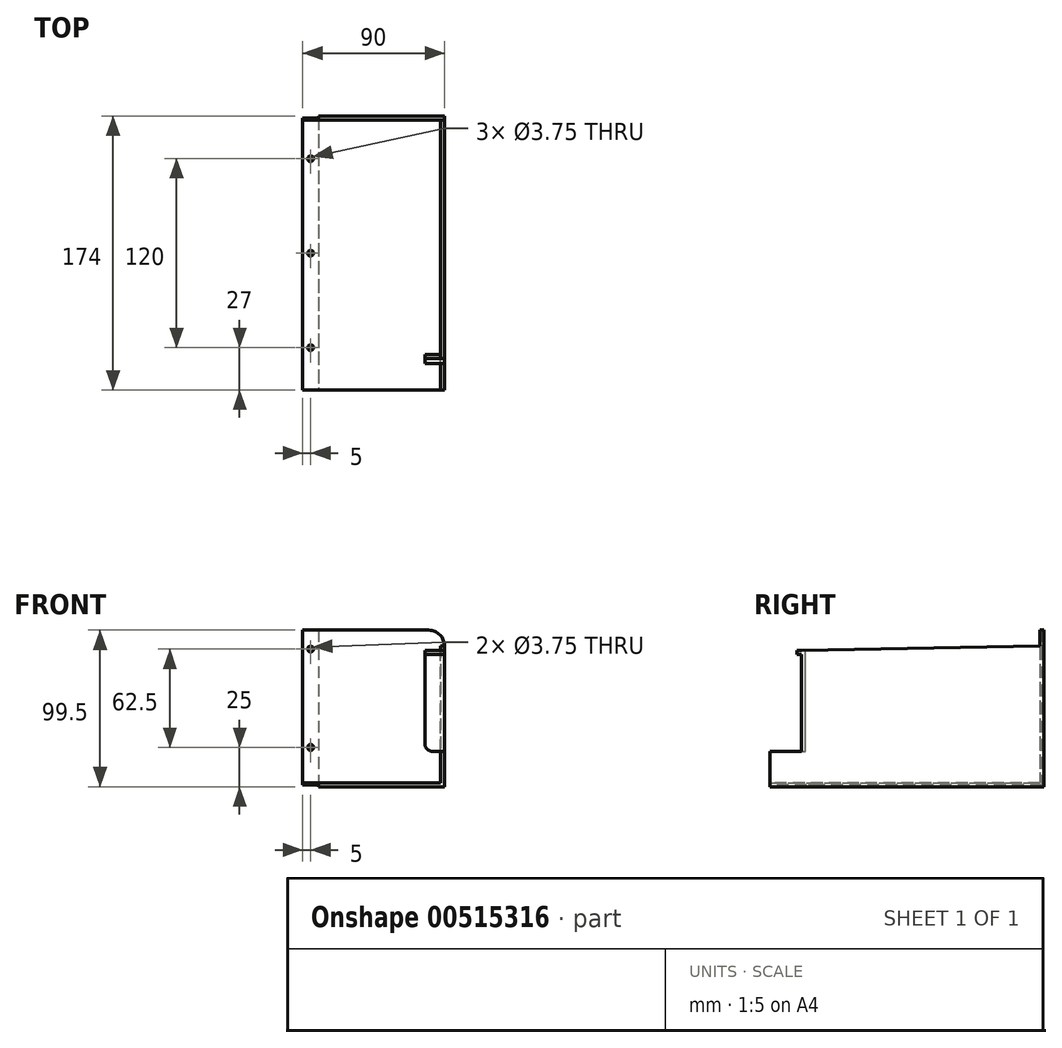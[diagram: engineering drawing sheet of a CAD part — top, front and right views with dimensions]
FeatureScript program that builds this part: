
annotation { "Feature Type Name" : "Feature", "Feature Type Description" : "" }
export const myFeature = defineFeature(function(context is Context, id is Id, definition is map)
    precondition{}
    {
        {
            var Q0;
            Q0=qCreatedBy(makeId("Top.planeOp"),FACE);
            var sketch = newSketch(context, id + "F0", { "sketchPlane" : qUnion([Q0])});
            skLineSegment(sketch, "E0.bottom", {"start": v(0, 87) * mm, "end": v(-80, 87) * mm});
            skLineSegment(sketch, "E0.top", {"start": v(0, -87) * mm, "end": v(-80, -87) * mm});
            skLineSegment(sketch, "E0.left", {"start": v(0, 87) * mm, "end": v(0, -87) * mm});
            skLineSegment(sketch, "E0.right", {"start": v(-80, 87) * mm, "end": v(-80, -87) * mm});
            skSolve(sketch);
        }
        {
            var Q0;
            Q0=qSketchRegion(id+"F0",true);
            extrude(context, id + "F1", {"entities" : qUnion([Q0]), "depth" : 2.5 * mm, "offsetDistance" : 25 * mm});
        }
        {
            var Q0;
            Q0=makeQuery(id+"F1.opExtrude","CAP_FACE",FACE,{"disambiguationData":[OSD([sQuery(id+"F0.wireOp",EDGE,"E0.bottom"),sQuery(id+"F0.wireOp",EDGE,"E0.top"),sQuery(id+"F0.wireOp",EDGE,"E0.left"),sQuery(id+"F0.wireOp",EDGE,"E0.right")])],"isStart":false});
            var sketch = newSketch(context, id + "F2", { "sketchPlane" : qUnion([Q0])});
            skLineSegment(sketch, "E1.bottom", {"start": v(-80, 87) * mm, "end": v(0, 87) * mm});
            skLineSegment(sketch, "E1.top", {"start": v(-80, 84.5) * mm, "end": v(0, 84.5) * mm});
            skLineSegment(sketch, "E1.left", {"start": v(-80, 87) * mm, "end": v(-80, 84.5) * mm});
            skLineSegment(sketch, "E1.right", {"start": v(0, 87) * mm, "end": v(0, 84.5) * mm});
            skSolve(sketch);
        }
        {
            var Q0;
            Q0=qSketchRegion(id+"F2",true);
            extrude(context, id + "F3", {"entities" : qUnion([Q0]), "operationType" : NewBodyOperationType.ADD, "depth" : 97 * mm, "offsetDistance" : 25 * mm});
        }
        {
            var Q0;
            Q0=makeQuery(id+"F3.boolean.opBoolean","MERGE",FACE,{"derivedFrom":[makeQuery(id+"F1.opExtrude","SWEPT_FACE",FACE,{"disambiguationData":[OSD([sQuery(id+"F0.wireOp",EDGE,"E0.right")])]}),makeQuery(id+"F3.opExtrude","SWEPT_FACE",FACE,{"disambiguationData":[OSD([sQuery(id+"F2.wireOp",EDGE,"E1.left")])]})]});
            var sketch = newSketch(context, id + "F4", { "sketchPlane" : qUnion([Q0])});
            skLineSegment(sketch, "E2", {"start": v(-84.5, 2.5) * mm, "end": v(-84.5, 89.5) * mm});
            skLineSegment(sketch, "E3", {"start": v(-84.5, 89.5) * mm, "end": v(67, 86.5) * mm});
            skLineSegment(sketch, "E4", {"start": v(67, 86.5) * mm, "end": v(67, 22.5) * mm});
            skLineSegment(sketch, "E5", {"start": v(87, 2.5) * mm, "end": v(-84.5, 2.5) * mm});
            skLineSegment(sketch, "E6", {"start": v(87, 2.5) * mm, "end": v(87, 22.5) * mm});
            skLineSegment(sketch, "E7", {"start": v(87, 22.5) * mm, "end": v(67, 22.5) * mm});
            skLineSegment(sketch, "E8", {"start": v(67, 22.5) * mm, "end": v(67, 22.5) * mm});
            skSolve(sketch);
        }
        {
            var Q0;
            Q0=qSketchRegion(id+"F4",true);
            extrude(context, id + "F5", {"entities" : qUnion([Q0]), "operationType" : NewBodyOperationType.ADD, "oppositeDirection" : true, "depth" : 2.5 * mm, "offsetDistance" : 25 * mm});
        }
        {
            var Q0;
            Q0=makeQuery(id+"F5.opExtrude","CAP_FACE",FACE,{"disambiguationData":[OSD([sQuery(id+"F4.wireOp",EDGE,"E2"),sQuery(id+"F4.wireOp",EDGE,"E3"),sQuery(id+"F4.wireOp",EDGE,"E4"),sQuery(id+"F4.wireOp",EDGE,"E5"),sQuery(id+"F4.wireOp",EDGE,"E6"),sQuery(id+"F4.wireOp",EDGE,"E7")])],"isStart":false});
            var sketch = newSketch(context, id + "F6", { "sketchPlane" : qUnion([Q0])});
            skLineSegment(sketch, "E9", {"start": v(-67, 86.5) * mm, "end": v(-67, 22.5) * mm});
            skLineSegment(sketch, "E10", {"start": v(-67, 22.5) * mm, "end": v(-64.5, 22.5) * mm});
            skLineSegment(sketch, "E11", {"start": v(-64.5, 22.5) * mm, "end": v(-64.5, 86.54) * mm});
            skLineSegment(sketch, "E12", {"start": v(-67, 86.5) * mm, "end": v(-64.5, 86.54) * mm});
            skSolve(sketch);
        }
        {
            var Q0;
            Q0=qSketchRegion(id+"F6",true);
            extrude(context, id + "F7", {"entities" : qUnion([Q0]), "operationType" : NewBodyOperationType.ADD, "depth" : 10 * mm, "offsetDistance" : 25 * mm});
        }
        {
            var Q0;
            Q0=makeQuery(id+"F7.boolean.opBoolean","MERGE",FACE,{"derivedFrom":[makeQuery(id+"F5.opExtrude","SWEPT_FACE",FACE,{"disambiguationData":[OSD([sQuery(id+"F4.wireOp",EDGE,"E4")])]}),makeQuery(id+"F7.opExtrude","SWEPT_FACE",FACE,{"disambiguationData":[OSD([sQuery(id+"F6.wireOp",EDGE,"E9")])]})]});
            var sketch = newSketch(context, id + "F8", { "sketchPlane" : qUnion([Q0])});
            skLineSegment(sketch, "E13.bottom", {"start": v(-67.5, 86.5) * mm, "end": v(-80, 86.5) * mm});
            skLineSegment(sketch, "E13.top", {"start": v(-67.5, 84) * mm, "end": v(-80, 84) * mm});
            skLineSegment(sketch, "E13.left", {"start": v(-67.5, 86.5) * mm, "end": v(-67.5, 84) * mm});
            skLineSegment(sketch, "E13.right", {"start": v(-80, 86.5) * mm, "end": v(-80, 84) * mm});
            skSolve(sketch);
        }
        {
            var Q0;
            Q0=qSketchRegion(id+"F8",true);
            extrude(context, id + "F9", {"entities" : qUnion([Q0]), "operationType" : NewBodyOperationType.ADD, "depth" : 3 * mm, "offsetDistance" : 25 * mm});
        }
        {
            var Q0;
            Q0=makeQuery(id+"F3.opExtrude","CAP_EDGE",EDGE,{"disambiguationData":[OSD([sQuery(id+"F2.wireOp",EDGE,"E1.left")])],"isStart":false});
            fillet(context, id + "F10", {"entities" : qUnion([Q0]), "radius" : 10 * mm, "tangentPropagation" : true, "allowEdgeOverflow" : false});
        }
        {
            var Q0;
            Q0=makeQuery(id+"F7.opExtrude","CAP_EDGE",EDGE,{"disambiguationData":[OSD([sQuery(id+"F6.wireOp",EDGE,"E10")])],"isStart":false});
            fillet(context, id + "F11", {"entities" : qUnion([Q0]), "radius" : 5 * mm, "tangentPropagation" : true, "allowEdgeOverflow" : false});
        }
        {
            var Q0;
            Q0=makeQuery(id+"F3.boolean.opBoolean","MERGE",FACE,{"derivedFrom":[makeQuery(id+"F1.opExtrude","SWEPT_FACE",FACE,{"disambiguationData":[OSD([sQuery(id+"F0.wireOp",EDGE,"E0.left")])]}),makeQuery(id+"F3.opExtrude","SWEPT_FACE",FACE,{"disambiguationData":[OSD([sQuery(id+"F2.wireOp",EDGE,"E1.right")])]})]});
            var sketch = newSketch(context, id + "F12", { "sketchPlane" : qUnion([Q0])});
            skLineSegment(sketch, "E14", {"start": v(85.75, 99.5) * mm, "end": v(85.75, 1.25) * mm});
            skLineSegment(sketch, "E15", {"start": v(85.75, 1.25) * mm, "end": v(-87, 1.25) * mm});
            skLineSegment(sketch, "E16", {"start": v(-87, 2.5) * mm, "end": v(84.5, 2.5) * mm});
            skLineSegment(sketch, "E17", {"start": v(84.5, 2.5) * mm, "end": v(84.5, 99.5) * mm});
            skLineSegment(sketch, "E18", {"start": v(84.5, 99.5) * mm, "end": v(85.75, 99.5) * mm});
            skLineSegment(sketch, "E19", {"start": v(-87, 1.25) * mm, "end": v(-87, 2.5) * mm});
            skSolve(sketch);
        }
        {
            var Q0;
            Q0=qSketchRegion(id+"F12",true);
            extrude(context, id + "F13", {"entities" : qUnion([Q0]), "operationType" : NewBodyOperationType.ADD, "depth" : 10 * mm, "offsetDistance" : 25 * mm});
        }
        {
            var Q0;
            Q0=makeQuery(id+"F1.opExtrude","SWEPT_BODY",BODY,{"disambiguationData":[OSD([sQuery(id+"F0.wireOp",EDGE,"E0.bottom"),sQuery(id+"F0.wireOp",EDGE,"E0.top"),sQuery(id+"F0.wireOp",EDGE,"E0.left"),sQuery(id+"F0.wireOp",EDGE,"E0.right")])]});
            var Q1;
            Q1=qCreatedBy(makeId("Right.planeOp"),FACE);
            mirror(context, id + "F14", {"entities" : qUnion([Q0]), "mirrorPlane" : qUnion([Q1])});
        }
        {
            var Q0;
            Q0=makeQuery(id+"F1.opExtrude","SWEPT_BODY",BODY,{"disambiguationData":[OSD([sQuery(id+"F0.wireOp",EDGE,"E0.bottom"),sQuery(id+"F0.wireOp",EDGE,"E0.top"),sQuery(id+"F0.wireOp",EDGE,"E0.left"),sQuery(id+"F0.wireOp",EDGE,"E0.right")])]});
            deleteBodies(context, id + "F15", {"entities" : qUnion([Q0])});
        }
        {
            var Q0;
            Q0=makeQuery(id+"F14.opPattern","COPY",FACE,{"derivedFrom":makeQuery(id+"F13.opExtrude","SWEPT_FACE",FACE,{"disambiguationData":[OSD([sQuery(id+"F12.wireOp",EDGE,"E15")])]}),"instanceName":"1"});
            var sketch = newSketch(context, id + "F16", { "sketchPlane" : qUnion([Q0])});
            skPoint(sketch, "E20", {"position": v(-5, -60) * mm});
            skPoint(sketch, "E21", {"position": v(-5, 60) * mm});
            skPoint(sketch, "E22", {"position": v(-5, 0) * mm});
            skSolve(sketch);
        }
        {
            var Q0;
            Q0=makeQuery(id+"F14.opPattern","COPY",FACE,{"derivedFrom":makeQuery(id+"F13.opExtrude","SWEPT_FACE",FACE,{"disambiguationData":[OSD([sQuery(id+"F12.wireOp",EDGE,"E14")])]}),"instanceName":"1"});
            var sketch = newSketch(context, id + "F17", { "sketchPlane" : qUnion([Q0])});
            skPoint(sketch, "E23", {"position": v(5, 87.5) * mm});
            skPoint(sketch, "E24", {"position": v(5, 25) * mm});
            skSolve(sketch);
        }
        {
            var Q0;
            Q0=sQuery(id+"F17.wireOp",VERTEX,"E23");
            var Q1;
            Q1=sQuery(id+"F17.wireOp",VERTEX,"E24");
            var Q2;
            Q2=sQuery(id+"F16.wireOp",VERTEX,"E20");
            var Q3;
            Q3=sQuery(id+"F16.wireOp",VERTEX,"E22");
            var Q4;
            Q4=sQuery(id+"F16.wireOp",VERTEX,"E21");
            var Q5;
            Q5=makeQuery(id+"F14.opPattern","COPY",BODY,{"derivedFrom":makeQuery(id+"F1.opExtrude","SWEPT_BODY",BODY,{"disambiguationData":[OSD([sQuery(id+"F0.wireOp",EDGE,"E0.bottom"),sQuery(id+"F0.wireOp",EDGE,"E0.top"),sQuery(id+"F0.wireOp",EDGE,"E0.left"),sQuery(id+"F0.wireOp",EDGE,"E0.right")])]}),"instanceName":"1"});
            hole(context, id + "F18", {"style" : HoleStyle.SIMPLE, "endStyle" : HoleEndStyle.BLIND, "holeDiameter" : 3.75 * mm, "majorDiameter" : 5 * mm, "holeDepth" : 4.5 * mm, "isTappedThrough" : true, "tappedDepth" : 12 * mm, "tapClearance" : 3, "locations" : qUnion([Q0, Q1, Q2, Q3, Q4]), "scope" : qUnion([Q5]), "startStyle" : HoleStartStyle.SKETCH});
        }
    });
